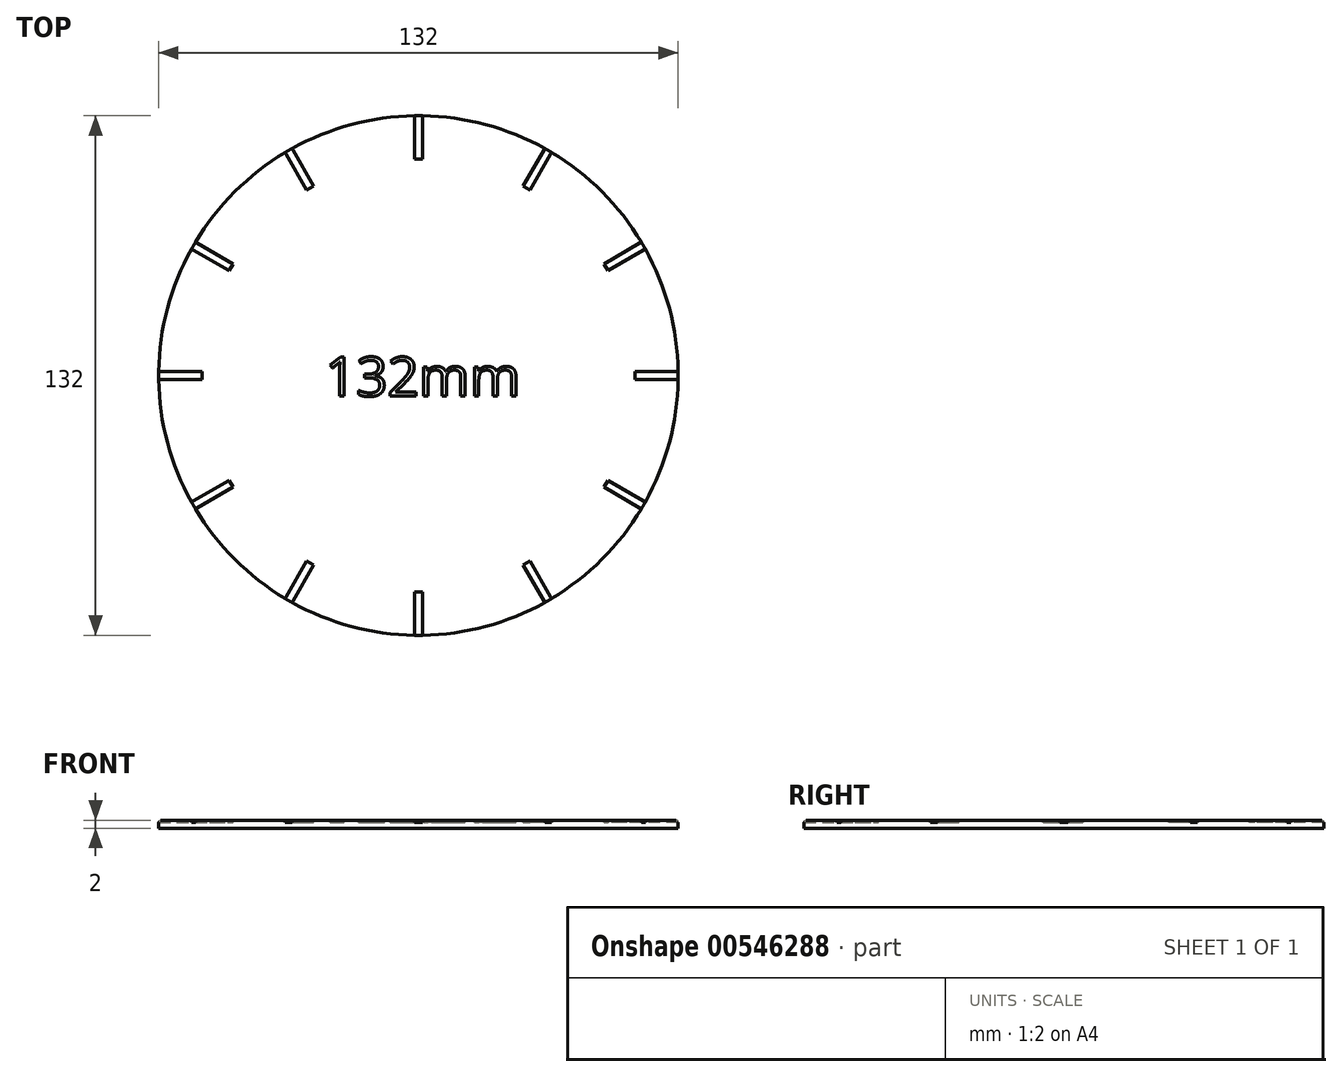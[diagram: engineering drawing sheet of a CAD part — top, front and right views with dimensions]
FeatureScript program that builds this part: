
annotation { "Feature Type Name" : "Feature", "Feature Type Description" : "" }
export const myFeature = defineFeature(function(context is Context, id is Id, definition is map)
    precondition{}
    {
        {
            var Q0;
            Q0=qCreatedBy(makeId("Top.planeOp"),FACE);
            var sketch = newSketch(context, id + "F0", { "sketchPlane" : qUnion([Q0])});
            skCircle(sketch, "E0", {"center": v(0, 0) * mm, "radius": 66 * mm});
            skSolve(sketch);
        }
        {
            var Q0;
            Q0=qSketchRegion(id+"F0",true);
            extrude(context, id + "F1", {"entities" : qUnion([Q0]), "depth" : 2 * mm, "offsetDistance" : 25 * mm});
        }
        {
            var Q0;
            Q0=makeQuery(id+"F1.opExtrude","CAP_FACE",FACE,{"disambiguationData":[OSD([sQuery(id+"F0.wireOp",EDGE,"E0")])],"isStart":false});
            var sketch = newSketch(context, id + "F2", { "sketchPlane" : qUnion([Q0])});
            skLineSegment(sketch, "E1.bottom", {"start": v(-1, 70) * mm, "end": v(1, 70) * mm});
            skLineSegment(sketch, "E1.top", {"start": v(-1, 55) * mm, "end": v(1, 55) * mm});
            skLineSegment(sketch, "E1.left", {"start": v(-1, 70) * mm, "end": v(-1, 55) * mm});
            skLineSegment(sketch, "E1.right", {"start": v(1, 70) * mm, "end": v(1, 55) * mm});
            skLineSegment(sketch, "E2.1.0", {"start": v(-35.87, 60.12) * mm, "end": v(-28.37, 47.13) * mm});
            skLineSegment(sketch, "E2.1.1", {"start": v(-34.13, 61.12) * mm, "end": v(-26.63, 48.13) * mm});
            skLineSegment(sketch, "E2.1.2", {"start": v(-28.37, 47.13) * mm, "end": v(-26.63, 48.13) * mm});
            skLineSegment(sketch, "E2.1.3", {"start": v(-35.87, 60.12) * mm, "end": v(-34.13, 61.12) * mm});
            skLineSegment(sketch, "E2.2.0", {"start": v(-61.12, 34.13) * mm, "end": v(-48.13, 26.63) * mm});
            skLineSegment(sketch, "E2.2.1", {"start": v(-60.12, 35.87) * mm, "end": v(-47.13, 28.37) * mm});
            skLineSegment(sketch, "E2.2.2", {"start": v(-48.13, 26.63) * mm, "end": v(-47.13, 28.37) * mm});
            skLineSegment(sketch, "E2.2.3", {"start": v(-61.12, 34.13) * mm, "end": v(-60.12, 35.87) * mm});
            skPoint(sketch, "E2.center", {"position": v(0, 0) * mm});
            skLineSegment(sketch, "E3.2.3.0", {"start": v(-70, -1) * mm, "end": v(-55, -1) * mm});
            skLineSegment(sketch, "E3.3.3.0", {"start": v(-70, 1) * mm, "end": v(-55, 1) * mm});
            skLineSegment(sketch, "E3.6.3.0", {"start": v(-55, -1) * mm, "end": v(-55, 1) * mm});
            skLineSegment(sketch, "E3.9.3.0", {"start": v(-70, -1) * mm, "end": v(-70, 1) * mm});
            skLineSegment(sketch, "E3.2.4.0", {"start": v(-60.12, -35.87) * mm, "end": v(-47.13, -28.37) * mm});
            skLineSegment(sketch, "E3.3.4.0", {"start": v(-61.12, -34.13) * mm, "end": v(-48.13, -26.63) * mm});
            skLineSegment(sketch, "E3.6.4.0", {"start": v(-47.13, -28.37) * mm, "end": v(-48.13, -26.63) * mm});
            skLineSegment(sketch, "E3.9.4.0", {"start": v(-60.12, -35.87) * mm, "end": v(-61.12, -34.13) * mm});
            skLineSegment(sketch, "E3.2.5.0", {"start": v(-34.13, -61.12) * mm, "end": v(-26.63, -48.13) * mm});
            skLineSegment(sketch, "E3.3.5.0", {"start": v(-35.87, -60.12) * mm, "end": v(-28.37, -47.13) * mm});
            skLineSegment(sketch, "E3.6.5.0", {"start": v(-26.63, -48.13) * mm, "end": v(-28.37, -47.13) * mm});
            skLineSegment(sketch, "E3.9.5.0", {"start": v(-34.13, -61.12) * mm, "end": v(-35.87, -60.12) * mm});
            skLineSegment(sketch, "E3.2.6.0", {"start": v(1, -70) * mm, "end": v(1, -55) * mm});
            skLineSegment(sketch, "E3.3.6.0", {"start": v(-1, -70) * mm, "end": v(-1, -55) * mm});
            skLineSegment(sketch, "E3.6.6.0", {"start": v(1, -55) * mm, "end": v(-1, -55) * mm});
            skLineSegment(sketch, "E3.9.6.0", {"start": v(1, -70) * mm, "end": v(-1, -70) * mm});
            skLineSegment(sketch, "E3.2.7.0", {"start": v(35.87, -60.12) * mm, "end": v(28.37, -47.13) * mm});
            skLineSegment(sketch, "E3.3.7.0", {"start": v(34.13, -61.12) * mm, "end": v(26.63, -48.13) * mm});
            skLineSegment(sketch, "E3.6.7.0", {"start": v(28.37, -47.13) * mm, "end": v(26.63, -48.13) * mm});
            skLineSegment(sketch, "E3.9.7.0", {"start": v(35.87, -60.12) * mm, "end": v(34.13, -61.12) * mm});
            skLineSegment(sketch, "E3.2.8.0", {"start": v(61.12, -34.13) * mm, "end": v(48.13, -26.63) * mm});
            skLineSegment(sketch, "E3.3.8.0", {"start": v(60.12, -35.87) * mm, "end": v(47.13, -28.37) * mm});
            skLineSegment(sketch, "E3.6.8.0", {"start": v(48.13, -26.63) * mm, "end": v(47.13, -28.37) * mm});
            skLineSegment(sketch, "E3.9.8.0", {"start": v(61.12, -34.13) * mm, "end": v(60.12, -35.87) * mm});
            skLineSegment(sketch, "E3.2.9.0", {"start": v(70, 1) * mm, "end": v(55, 1) * mm});
            skLineSegment(sketch, "E3.3.9.0", {"start": v(70, -1) * mm, "end": v(55, -1) * mm});
            skLineSegment(sketch, "E3.6.9.0", {"start": v(55, 1) * mm, "end": v(55, -1) * mm});
            skLineSegment(sketch, "E3.9.9.0", {"start": v(70, 1) * mm, "end": v(70, -1) * mm});
            skLineSegment(sketch, "E3.2.10.0", {"start": v(60.12, 35.87) * mm, "end": v(47.13, 28.37) * mm});
            skLineSegment(sketch, "E3.3.10.0", {"start": v(61.12, 34.13) * mm, "end": v(48.13, 26.63) * mm});
            skLineSegment(sketch, "E3.6.10.0", {"start": v(47.13, 28.37) * mm, "end": v(48.13, 26.63) * mm});
            skLineSegment(sketch, "E3.9.10.0", {"start": v(60.12, 35.87) * mm, "end": v(61.12, 34.13) * mm});
            skLineSegment(sketch, "E3.2.11.0", {"start": v(34.13, 61.12) * mm, "end": v(26.63, 48.13) * mm});
            skLineSegment(sketch, "E3.3.11.0", {"start": v(35.87, 60.12) * mm, "end": v(28.37, 47.13) * mm});
            skLineSegment(sketch, "E3.6.11.0", {"start": v(26.63, 48.13) * mm, "end": v(28.37, 47.13) * mm});
            skLineSegment(sketch, "E3.9.11.0", {"start": v(34.13, 61.12) * mm, "end": v(35.87, 60.12) * mm});
            skSolve(sketch);
        }
        {
            var Q0;
            Q0=qSketchRegion(id+"F2",true);
            extrude(context, id + "F3", {"entities" : qUnion([Q0]), "operationType" : NewBodyOperationType.REMOVE, "oppositeDirection" : true, "depth" : .5 * mm, "offsetDistance" : 25 * mm});
        }
        {
            var Q0;
            Q0=makeQuery(id+"F1.opExtrude","CAP_FACE",FACE,{"disambiguationData":[OSD([sQuery(id+"F0.wireOp",EDGE,"E0")])],"isStart":false});
            var sketch = newSketch(context, id + "F4", { "sketchPlane" : qUnion([Q0])});
            skText(sketch, "E4", { "text": "132mm\n", "fontName": "OpenSans-Regular.ttf"});
            const initialGuessF4  = {"E4": [-0.02373, -0.00525, 1, 0, 0.01]};
            skSetInitialGuess(sketch, initialGuessF4);
            skSolve(sketch);
        }
        {
            var Q0;
            Q0=qSketchRegion(id+"F4",true);
            extrude(context, id + "F5", {"entities" : qUnion([Q0]), "operationType" : NewBodyOperationType.REMOVE, "oppositeDirection" : true, "depth" : .5 * mm, "offsetDistance" : 25 * mm});
        }
        {
            var Q0;
            {var subQ0=sQuery(id+"F0.wireOp",EDGE,"E0");Q0=makeQuery(id+"F3.boolean.opBoolean","SPLIT",EDGE,{"disambiguationData":[TD([makeQuery(id+"F3.opExtrude","SWEPT_FACE",FACE,{"disambiguationData":[OSD([sQuery(id+"F2.wireOp",EDGE,"E3.2.10.0")])]})])],"derivedFrom":makeQuery(id+"F1.opExtrude","CAP_EDGE",EDGE,{"disambiguationData":[OSD([subQ0])],"isStart":false})});}
            var Q1;
            {var subQ0=sQuery(id+"F0.wireOp",EDGE,"E0");Q1=makeQuery(id+"F3.boolean.opBoolean","SPLIT",EDGE,{"disambiguationData":[TD([makeQuery(id+"F3.opExtrude","SWEPT_FACE",FACE,{"disambiguationData":[OSD([sQuery(id+"F2.wireOp",EDGE,"E3.2.9.0")])]})])],"derivedFrom":makeQuery(id+"F1.opExtrude","CAP_EDGE",EDGE,{"disambiguationData":[OSD([subQ0])],"isStart":false})});}
            var Q2;
            {var subQ0=sQuery(id+"F0.wireOp",EDGE,"E0");Q2=makeQuery(id+"F3.boolean.opBoolean","SPLIT",EDGE,{"disambiguationData":[TD([makeQuery(id+"F3.opExtrude","SWEPT_FACE",FACE,{"disambiguationData":[OSD([sQuery(id+"F2.wireOp",EDGE,"E3.2.8.0")])]})])],"derivedFrom":makeQuery(id+"F1.opExtrude","CAP_EDGE",EDGE,{"disambiguationData":[OSD([subQ0])],"isStart":false})});}
            var Q3;
            {var subQ0=sQuery(id+"F0.wireOp",EDGE,"E0");Q3=makeQuery(id+"F3.boolean.opBoolean","SPLIT",EDGE,{"disambiguationData":[TD([makeQuery(id+"F3.opExtrude","SWEPT_FACE",FACE,{"disambiguationData":[OSD([sQuery(id+"F2.wireOp",EDGE,"E3.2.7.0")])]})])],"derivedFrom":makeQuery(id+"F1.opExtrude","CAP_EDGE",EDGE,{"disambiguationData":[OSD([subQ0])],"isStart":false})});}
            var Q4;
            {var subQ0=sQuery(id+"F0.wireOp",EDGE,"E0");Q4=makeQuery(id+"F3.boolean.opBoolean","SPLIT",EDGE,{"disambiguationData":[TD([makeQuery(id+"F3.opExtrude","SWEPT_FACE",FACE,{"disambiguationData":[OSD([sQuery(id+"F2.wireOp",EDGE,"E3.2.6.0")])]})])],"derivedFrom":makeQuery(id+"F1.opExtrude","CAP_EDGE",EDGE,{"disambiguationData":[OSD([subQ0])],"isStart":false})});}
            var Q5;
            {var subQ0=sQuery(id+"F0.wireOp",EDGE,"E0");Q5=makeQuery(id+"F3.boolean.opBoolean","SPLIT",EDGE,{"disambiguationData":[TD([makeQuery(id+"F3.opExtrude","SWEPT_FACE",FACE,{"disambiguationData":[OSD([sQuery(id+"F2.wireOp",EDGE,"E3.2.5.0")])]})])],"derivedFrom":makeQuery(id+"F1.opExtrude","CAP_EDGE",EDGE,{"disambiguationData":[OSD([subQ0])],"isStart":false})});}
            var Q6;
            {var subQ0=sQuery(id+"F0.wireOp",EDGE,"E0");Q6=makeQuery(id+"F3.boolean.opBoolean","SPLIT",EDGE,{"disambiguationData":[TD([makeQuery(id+"F3.opExtrude","SWEPT_FACE",FACE,{"disambiguationData":[OSD([sQuery(id+"F2.wireOp",EDGE,"E3.2.4.0")])]})])],"derivedFrom":makeQuery(id+"F1.opExtrude","CAP_EDGE",EDGE,{"disambiguationData":[OSD([subQ0])],"isStart":false})});}
            var Q7;
            {var subQ0=sQuery(id+"F0.wireOp",EDGE,"E0");Q7=makeQuery(id+"F3.boolean.opBoolean","SPLIT",EDGE,{"disambiguationData":[TD([makeQuery(id+"F3.opExtrude","SWEPT_FACE",FACE,{"disambiguationData":[OSD([sQuery(id+"F2.wireOp",EDGE,"E3.2.3.0")])]})])],"derivedFrom":makeQuery(id+"F1.opExtrude","CAP_EDGE",EDGE,{"disambiguationData":[OSD([subQ0])],"isStart":false})});}
            var Q8;
            {var subQ0=sQuery(id+"F0.wireOp",EDGE,"E0");Q8=makeQuery(id+"F3.boolean.opBoolean","SPLIT",EDGE,{"disambiguationData":[TD([makeQuery(id+"F3.opExtrude","SWEPT_FACE",FACE,{"disambiguationData":[OSD([sQuery(id+"F2.wireOp",EDGE,"E2.2.0")])]})])],"derivedFrom":makeQuery(id+"F1.opExtrude","CAP_EDGE",EDGE,{"disambiguationData":[OSD([subQ0])],"isStart":false})});}
            var Q9;
            {var subQ0=sQuery(id+"F0.wireOp",EDGE,"E0");Q9=makeQuery(id+"F3.boolean.opBoolean","SPLIT",EDGE,{"disambiguationData":[TD([makeQuery(id+"F3.opExtrude","SWEPT_FACE",FACE,{"disambiguationData":[OSD([sQuery(id+"F2.wireOp",EDGE,"E2.1.0")])]})])],"derivedFrom":makeQuery(id+"F1.opExtrude","CAP_EDGE",EDGE,{"disambiguationData":[OSD([subQ0])],"isStart":false})});}
            var Q10;
            {var subQ0=sQuery(id+"F0.wireOp",EDGE,"E0");Q10=makeQuery(id+"F3.boolean.opBoolean","SPLIT",EDGE,{"disambiguationData":[TD([makeQuery(id+"F3.opExtrude","SWEPT_FACE",FACE,{"disambiguationData":[OSD([sQuery(id+"F2.wireOp",EDGE,"E1.left")])]})])],"derivedFrom":makeQuery(id+"F1.opExtrude","CAP_EDGE",EDGE,{"disambiguationData":[OSD([subQ0])],"isStart":false})});}
            var Q11;
            {var subQ0=sQuery(id+"F0.wireOp",EDGE,"E0");Q11=makeQuery(id+"F3.boolean.opBoolean","SPLIT",EDGE,{"disambiguationData":[TD([makeQuery(id+"F3.opExtrude","SWEPT_FACE",FACE,{"disambiguationData":[OSD([sQuery(id+"F2.wireOp",EDGE,"E1.right")])]})])],"derivedFrom":makeQuery(id+"F1.opExtrude","CAP_EDGE",EDGE,{"disambiguationData":[OSD([subQ0])],"isStart":false})});}
            fillet(context, id + "F6", {"entities" : qUnion([Q0, Q1, Q2, Q3, Q4, Q5, Q6, Q7, Q8, Q9, Q10, Q11]), "radius" : .5 * mm, "tangentPropagation" : true, "allowEdgeOverflow" : false});
        }
    });
